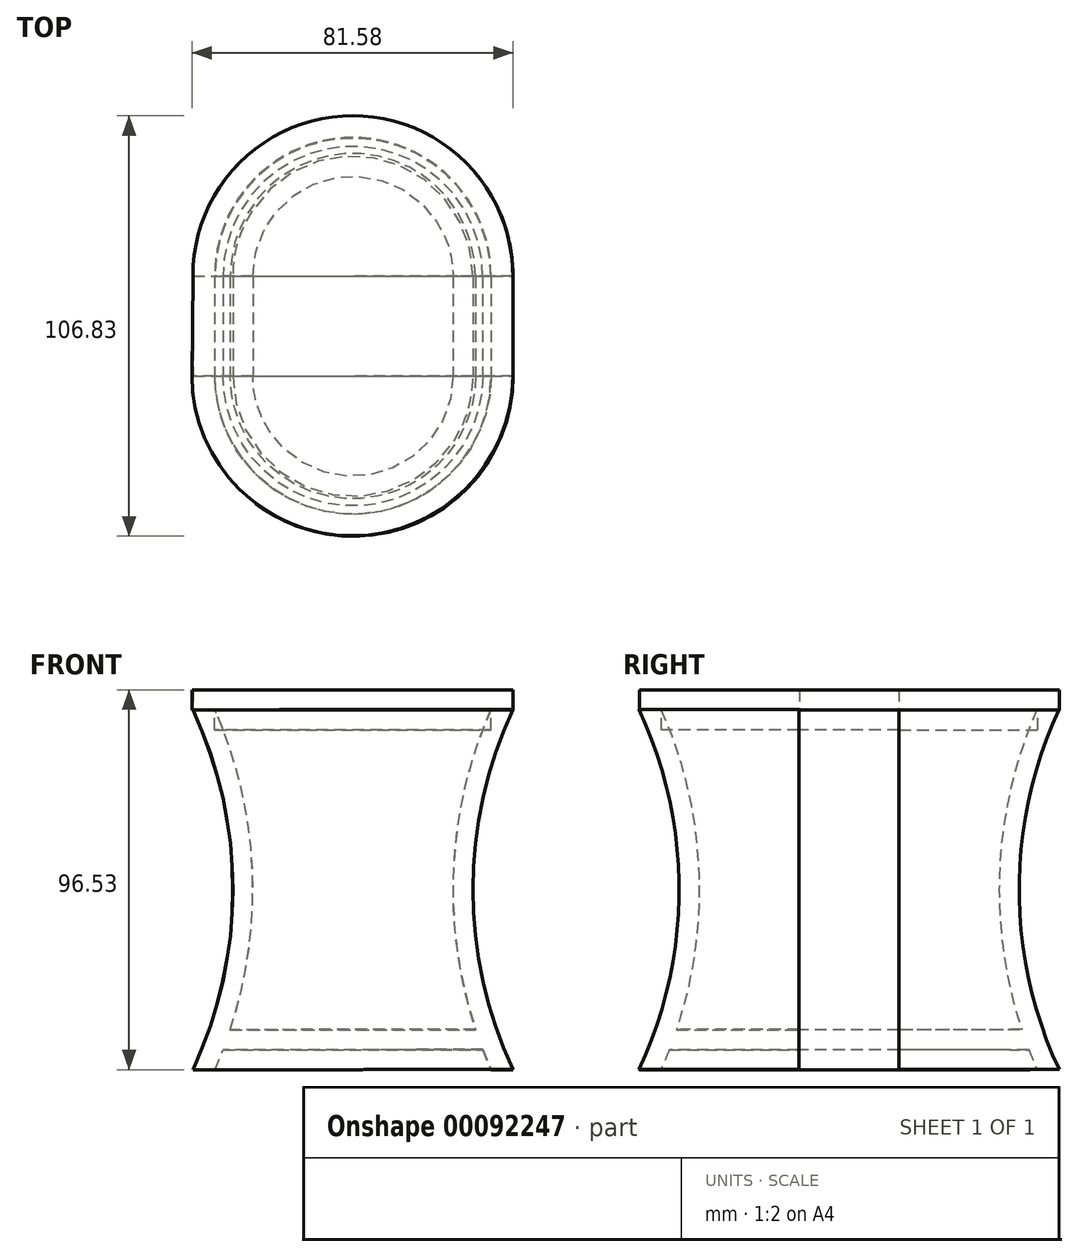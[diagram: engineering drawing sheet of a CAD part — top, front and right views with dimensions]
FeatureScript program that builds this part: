
annotation { "Feature Type Name" : "Feature", "Feature Type Description" : "" }
export const myFeature = defineFeature(function(context is Context, id is Id, definition is map)
    precondition{}
    {
        {
            var Q0;
            Q0=qCreatedBy(makeId("Front.planeOp"),FACE);
            var sketch = newSketch(context, id + "F0", { "sketchPlane" : qUnion([Q0])});
            skArc(sketch, "E0.MirrorCS", {"start": v(-40.64, 45.72) * mm, "mid": v(-30.48, 0) * mm, "end": v(-40.64, -45.72) * mm});
            skArc(sketch, "E1.0", {"start": v(-35.06, 45.72) * mm, "mid": v(-25.4, 0) * mm, "end": v(-35.06, -45.72) * mm});
            skLineSegment(sketch, "E2", {"start": v(-40.64, 45.72) * mm, "end": v(-35.06, 45.72) * mm});
            skLineSegment(sketch, "E3", {"start": v(-40.64, -45.72) * mm, "end": v(-35.06, -45.72) * mm});
            skLineSegment(sketch, "E4", {"start": v(-31.14, -35.56) * mm, "end": v(0.02, -35.56) * mm});
            skLineSegment(sketch, "E5", {"start": v(0, 59) * mm, "end": v(0.03, -60.15) * mm});
            skPoint(sketch, "E5.endSnap0", {"position": v(0.03, -40.64) * mm});
            skLineSegment(sketch, "E6", {"start": v(0.03, -40.64) * mm, "end": v(-32.96, -40.65) * mm});
            skSolve(sketch);
        }
        {
            var Q0;
            Q0=qCreatedBy(makeId("Front.planeOp"),FACE);
            cPlane(context, id + "F1", {"entities" : qUnion([Q0]), "cplaneType" : CPlaneType.OFFSET, "offset" : 25.4 * mm, "width" : 152.4 * mm, "height" : 152.4 * mm});
        }
        {
            var Q0;
            Q0=qCreatedBy(id+"F1.planeOp",FACE);
            var sketch = newSketch(context, id + "F2", { "sketchPlane" : qUnion([Q0])});
            skArc(sketch, "E7", {"start": v(40.64, 45.72) * mm, "mid": v(30.48, 0) * mm, "end": v(40.64, -45.72) * mm});
            skArc(sketch, "E8.MirrorCS", {"start": v(-40.64, 45.72) * mm, "mid": v(-30.48, 0) * mm, "end": v(-40.64, -45.72) * mm});
            skArc(sketch, "E9.0", {"start": v(-35.06, 45.72) * mm, "mid": v(-25.4, 0) * mm, "end": v(-35.06, -45.72) * mm});
            skArc(sketch, "E10.MirrorCS", {"start": v(35.06, 45.72) * mm, "mid": v(25.4, 0) * mm, "end": v(35.06, -45.72) * mm});
            skLineSegment(sketch, "E11", {"start": v(-40.64, 45.72) * mm, "end": v(-35.06, 45.72) * mm});
            skLineSegment(sketch, "E12", {"start": v(-40.64, -45.72) * mm, "end": v(-35.06, -45.72) * mm});
            skLineSegment(sketch, "E13", {"start": v(35.06, -45.72) * mm, "end": v(40.64, -45.72) * mm});
            skLineSegment(sketch, "E14", {"start": v(35.06, 45.72) * mm, "end": v(40.64, 45.72) * mm});
            skLineSegment(sketch, "E15", {"start": v(-32.96, -40.64) * mm, "end": v(32.96, -40.64) * mm});
            skLineSegment(sketch, "E16", {"start": v(-31.14, -35.56) * mm, "end": v(31.14, -35.56) * mm});
            skSolve(sketch);
        }
        {
            var Q0;
            Q0 = qSketchRegion(id + "F2", true);
            extrude(context, id + "F3", {"entities" : qUnion([Q0]), "oppositeDirection" : true, "depth" : 25.4 * mm});
        }
        {
            var Q0;
            Q0 = qSketchRegion(id + "F0", true);
            var Q1;
            Q1=sQuery(id+"F0.wireOp",EDGE,"E5");
            revolve(context, id + "F4", {"entities" : qUnion([Q0]), "axis" : qUnion([Q1]), "revolveType" : RevolveType.ONE_DIRECTION, "angle" : 180 * degree});
        }
        {
            var Q0;
            Q0=qCreatedBy(id+"F1.planeOp",FACE);
            var sketch = newSketch(context, id + "F5", { "sketchPlane" : qUnion([Q0])});
            skArc(sketch, "E17.MirrorCS", {"start": v(-40.63, 45.72) * mm, "mid": v(-30.46, 0) * mm, "end": v(-40.62, -45.73) * mm});
            skArc(sketch, "E18.0", {"start": v(-35.04, 45.71) * mm, "mid": v(-25.38, 0) * mm, "end": v(-35.04, -45.73) * mm});
            skLineSegment(sketch, "E19", {"start": v(-40.63, 45.72) * mm, "end": v(-35.04, 45.71) * mm});
            skLineSegment(sketch, "E20", {"start": v(-40.62, -45.73) * mm, "end": v(-35.04, -45.73) * mm});
            skLineSegment(sketch, "E21", {"start": v(-31.12, -35.57) * mm, "end": v(0.04, -35.57) * mm});
            skLineSegment(sketch, "E22", {"start": v(0.02, 59) * mm, "end": v(0.05, -60.16) * mm});
            skPoint(sketch, "E22.endSnap0", {"position": v(0.05, -40.65) * mm});
            skLineSegment(sketch, "E23", {"start": v(0.05, -40.65) * mm, "end": v(-32.95, -40.65) * mm});
            skSolve(sketch);
        }
        {
            var Q0;
            Q0 = qSketchRegion(id + "F5", true);
            var Q1;
            Q1=sQuery(id+"F5.wireOp",EDGE,"E22");
            revolve(context, id + "F6", {"entities" : qUnion([Q0]), "axis" : qUnion([Q1]), "revolveType" : RevolveType.ONE_DIRECTION, "oppositeDirection" : true, "angle" : 180 * degree});
        }
        {
            var Q0;
            Q0=qCreatedBy(makeId("Top.planeOp"),FACE);
            cPlane(context, id + "F7", {"entities" : qUnion([Q0]), "cplaneType" : CPlaneType.OFFSET, "offset" : 45.72 * mm, "width" : 152.4 * mm, "height" : 152.4 * mm});
        }
        {
            var Q0;
            Q0=qCreatedBy(id+"F7.planeOp",FACE);
            var sketch = newSketch(context, id + "F8", { "sketchPlane" : qUnion([Q0])});
            skArc(sketch, "E24", {"start": v(35.1, 0) * mm, "mid": v(0, 35.21) * mm, "end": v(-35.1, 0) * mm});
            skArc(sketch, "E25", {"start": v(-35.1, -25.05) * mm, "mid": v(-0.12, -60.38) * mm, "end": v(35.1, -25.28) * mm});
            skLineSegment(sketch, "E26", {"start": v(-35.1, 0) * mm, "end": v(-35.1, -25.05) * mm});
            skLineSegment(sketch, "E27", {"start": v(35.1, 0) * mm, "end": v(35.1, -25.28) * mm});
            skSolve(sketch);
        }
        {
            var Q0;
            Q0 = qSketchRegion(id + "F8", true);
            extrude(context, id + "F9", {"entities" : qUnion([Q0]), "oppositeDirection" : true, "depth" : 5.08 * mm});
        }
        {
            var Q0;
            Q0=makeQuery(id+"F3.opExtrude","SWEPT_BODY",BODY,{"disambiguationData":[OSD([sQuery(id+"F2.wireOp",EDGE,"E7"),sQuery(id+"F2.wireOp",EDGE,"E8.MirrorCS"),sQuery(id+"F2.wireOp",EDGE,"E9.0"),sQuery(id+"F2.wireOp",EDGE,"E10.MirrorCS"),sQuery(id+"F2.wireOp",EDGE,"E11"),sQuery(id+"F2.wireOp",EDGE,"E12"),sQuery(id+"F2.wireOp",EDGE,"E13"),sQuery(id+"F2.wireOp",EDGE,"E14"),sQuery(id+"F2.wireOp",EDGE,"E15"),sQuery(id+"F2.wireOp",EDGE,"E16")])]});
            transform(context, id + "F10", {"entities" : qUnion([Q0]), "transformType" : TransformType.TRANSLATION_3D, "dx" : 0 * mm, "dy" : 0 * mm, "dz" : 0 * mm, "makeCopy" : true});
        }
        {
            var Q0;
            Q0=qCreatedBy(id+"F7.planeOp",FACE);
            var sketch = newSketch(context, id + "F11", { "sketchPlane" : qUnion([Q0])});
            skArc(sketch, "E28", {"start": v(40.64, 0) * mm, "mid": v(0, 40.76) * mm, "end": v(-40.64, 0) * mm});
            skArc(sketch, "E29", {"start": v(-40.87, -25.28) * mm, "mid": v(-0.12, -65.92) * mm, "end": v(40.64, -25.28) * mm});
            skLineSegment(sketch, "E30", {"start": v(-40.87, -25.28) * mm, "end": v(-40.64, 0) * mm});
            skLineSegment(sketch, "E31", {"start": v(40.64, -25.28) * mm, "end": v(40.64, 0) * mm});
            skSolve(sketch);
        }
        {
            var Q0;
            Q0 = qSketchRegion(id + "F11", true);
            extrude(context, id + "F12", {"entities" : qUnion([Q0]), "depth" : 5.08 * mm});
        }
        {
            var Q0;
            Q0=makeQuery(id+"F10.opPattern","COPY",BODY,{"derivedFrom":makeQuery(id+"F3.opExtrude","SWEPT_BODY",BODY,{"disambiguationData":[OSD([sQuery(id+"F2.wireOp",EDGE,"E7"),sQuery(id+"F2.wireOp",EDGE,"E8.MirrorCS"),sQuery(id+"F2.wireOp",EDGE,"E9.0"),sQuery(id+"F2.wireOp",EDGE,"E10.MirrorCS"),sQuery(id+"F2.wireOp",EDGE,"E11"),sQuery(id+"F2.wireOp",EDGE,"E12"),sQuery(id+"F2.wireOp",EDGE,"E13"),sQuery(id+"F2.wireOp",EDGE,"E14"),sQuery(id+"F2.wireOp",EDGE,"E15"),sQuery(id+"F2.wireOp",EDGE,"E16")])]}),"instanceName":"1"});
            var Q1;
            Q1=makeQuery(id+"F9.opExtrude","SWEPT_BODY",BODY,{"disambiguationData":[OSD([sQuery(id+"F8.wireOp",EDGE,"E24"),sQuery(id+"F8.wireOp",EDGE,"E25"),sQuery(id+"F8.wireOp",EDGE,"E26"),sQuery(id+"F8.wireOp",EDGE,"E27")])]});
            booleanBodies(context, id + "F13", {"operationType" : BooleanOperationType.SUBTRACTION, "tools" : qUnion([Q0]), "targets" : qUnion([Q1])});
        }
    });
